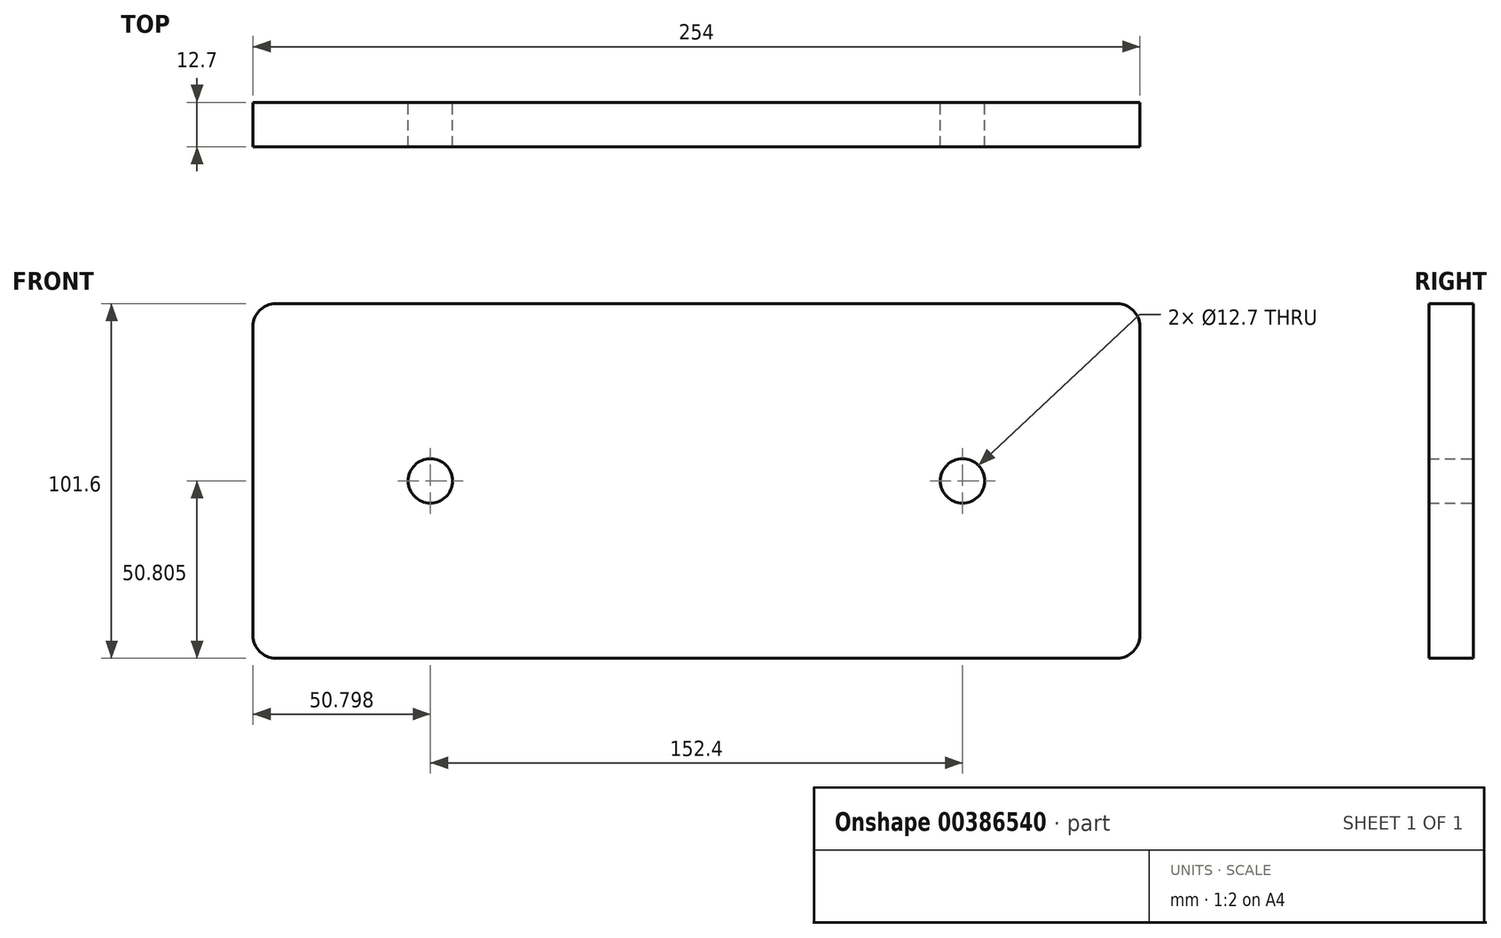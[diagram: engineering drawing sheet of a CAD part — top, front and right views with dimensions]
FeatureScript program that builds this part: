
annotation { "Feature Type Name" : "Feature", "Feature Type Description" : "" }
export const myFeature = defineFeature(function(context is Context, id is Id, definition is map)
    precondition{}
    {
        {
            var Q0;
            Q0=qCreatedBy(makeId("Front.planeOp"),FACE);
            var sketch = newSketch(context, id + "F0", { "sketchPlane" : qUnion([Q0])});
            skLineSegment(sketch, "E0.bottom", {"start": v(-127.76, 42.75) * mm, "end": v(126.24, 42.75) * mm});
            skLineSegment(sketch, "E0.top", {"start": v(-127.76, -58.85) * mm, "end": v(126.24, -58.85) * mm});
            skLineSegment(sketch, "E0.left", {"start": v(-127.76, 42.75) * mm, "end": v(-127.76, -58.85) * mm});
            skLineSegment(sketch, "E0.right", {"start": v(126.24, 42.75) * mm, "end": v(126.24, -58.85) * mm});
            skPoint(sketch, "E1", {"position": v(-76.96, -8.05) * mm});
            skPoint(sketch, "E2", {"position": v(75.44, -8.05) * mm});
            skSolve(sketch);
        }
        {
            var Q0;
            Q0 = qSketchRegion(id + "F0", true);
            extrude(context, id + "F1", {"entities" : qUnion([Q0]), "depth" : 12.7 * mm});
        }
        {
            var Q0;
            Q0=makeQuery(id+"F1.opExtrude","SWEPT_EDGE",EDGE,{"disambiguationData":[OSD([sQuery(id+"F0.wireOp",EDGE,"E0.bottom"),sQuery(id+"F0.wireOp",EDGE,"E0.left")])]});
            var Q1;
            Q1=makeQuery(id+"F1.opExtrude","SWEPT_EDGE",EDGE,{"disambiguationData":[OSD([sQuery(id+"F0.wireOp",EDGE,"E0.top"),sQuery(id+"F0.wireOp",EDGE,"E0.left")])]});
            var Q2;
            Q2=makeQuery(id+"F1.opExtrude","SWEPT_EDGE",EDGE,{"disambiguationData":[OSD([sQuery(id+"F0.wireOp",EDGE,"E0.top"),sQuery(id+"F0.wireOp",EDGE,"E0.right")])]});
            var Q3;
            Q3=makeQuery(id+"F1.opExtrude","SWEPT_EDGE",EDGE,{"disambiguationData":[OSD([sQuery(id+"F0.wireOp",EDGE,"E0.bottom"),sQuery(id+"F0.wireOp",EDGE,"E0.right")])]});
            fillet(context, id + "F2", {"entities" : qUnion([Q0, Q1, Q2, Q3]), "radius" : 6.55 * mm, "tangentPropagation" : true, "allowEdgeOverflow" : false});
        }
        {
            var Q0;
            Q0=sQuery(id+"F0.wireOp",VERTEX,"E1");
            var Q1;
            Q1=sQuery(id+"F0.wireOp",VERTEX,"E2");
            var Q2;
            Q2=makeQuery(id+"F1.opExtrude","SWEPT_BODY",BODY,{"disambiguationData":[OSD([sQuery(id+"F0.wireOp",EDGE,"E0.bottom"),sQuery(id+"F0.wireOp",EDGE,"E0.top"),sQuery(id+"F0.wireOp",EDGE,"E0.left"),sQuery(id+"F0.wireOp",EDGE,"E0.right")])]});
            hole(context, id + "F3", {"style" : HoleStyle.SIMPLE, "endStyle" : HoleEndStyle.THROUGH, "oppositeDirection" : true, "holeDiameter" : 12.7 * mm, "isTappedThrough" : true, "tappedDepth" : 12.7 * mm, "tapClearance" : 3, "startFromSketch" : true, "locations" : qUnion([Q0, Q1]), "scope" : qUnion([Q2])});
        }
    });
